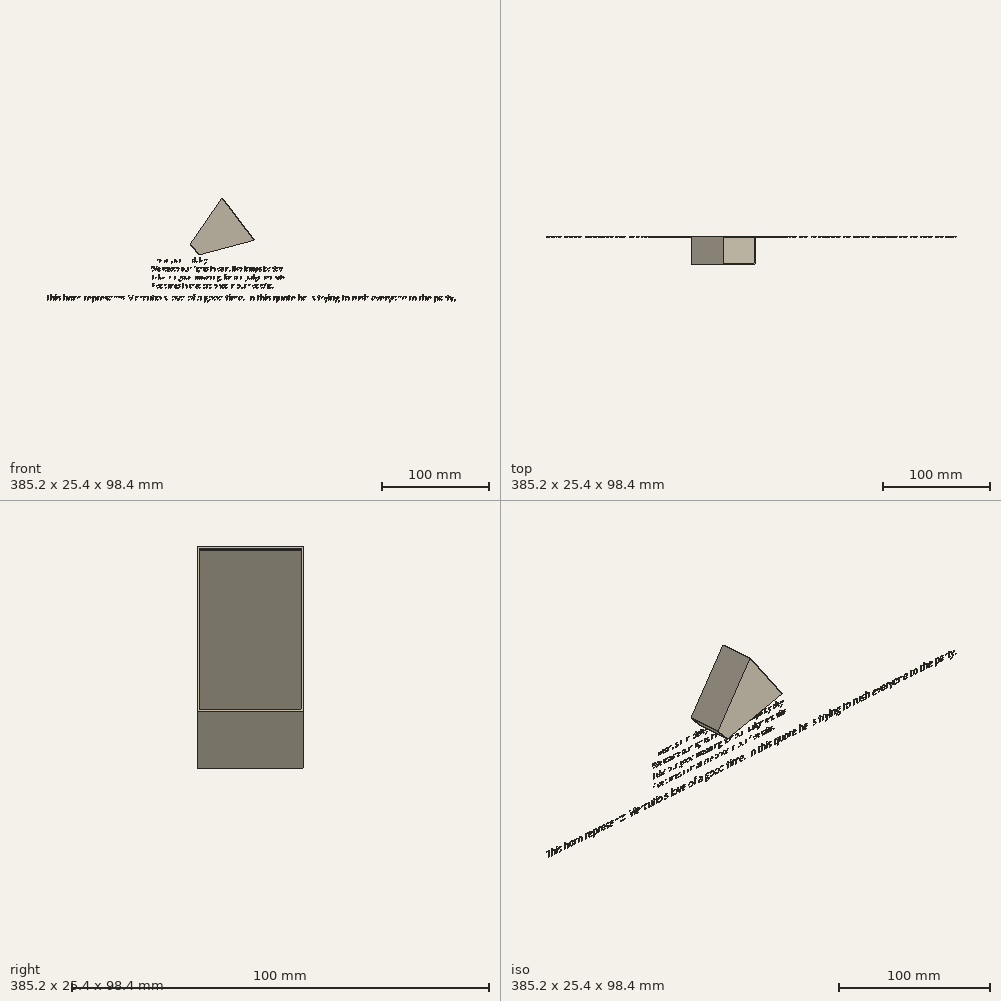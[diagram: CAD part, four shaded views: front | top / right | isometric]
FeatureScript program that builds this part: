
annotation { "Feature Type Name" : "Feature", "Feature Type Description" : "" }
export const myFeature = defineFeature(function(context is Context, id is Id, definition is map)
    precondition{}
    {
        {
            var Q0;
            Q0=qCreatedBy(makeId("Front.planeOp"),FACE);
            var sketch = newSketch(context, id + "F0", { "sketchPlane" : qUnion([Q0])});
            skLineSegment(sketch, "E0", {"start": v(-35.2, 9.6) * mm, "end": v(-26.26, 0) * mm});
            skLineSegment(sketch, "E1", {"start": v(-4.95, 53.37) * mm, "end": v(25.14, 13.72) * mm});
            skLineSegment(sketch, "E2", {"start": v(25.14, 13.72) * mm, "end": v(-26.26, 0) * mm});
            skLineSegment(sketch, "E3", {"start": v(-35.2, 9.6) * mm, "end": v(-4.95, 53.37) * mm});
            skSolve(sketch);
        }
        {
            var Q0;
            Q0=makeQuery(id+"F0.imprint","IMPRINT",FACE,{"disambiguationData":[TD([[makeQuery(id+"F0.imprint","IMPRINT",EDGE,{"derivedFrom":sQuery(id+"F0.wireOp",EDGE,"E0")}),1.0]])]});
            extrude(context, id + "F1", {"entities" : qUnion([Q0]), "depth" : 25.4 * mm, "offsetDistance" : 25.4 * mm});
        }
        {
            var Q0;
            Q0=makeQuery(id+"F1.opExtrude","CAP_FACE",FACE,{"disambiguationData":[OSD([sQuery(id+"F0.wireOp",EDGE,"E0"),sQuery(id+"F0.wireOp",EDGE,"E1"),sQuery(id+"F0.wireOp",EDGE,"E2"),sQuery(id+"F0.wireOp",EDGE,"E3")])],"isStart":false});
            var Q1;
            Q1=makeQuery(id+"F1.opExtrude","SWEPT_FACE",FACE,{"disambiguationData":[OSD([sQuery(id+"F0.wireOp",EDGE,"E1")])]});
            var Q2;
            Q2=makeQuery(id+"F1.opExtrude","SWEPT_FACE",FACE,{"disambiguationData":[OSD([sQuery(id+"F0.wireOp",EDGE,"E2")])]});
            var Q3;
            Q3=makeQuery(id+"F1.opExtrude","SWEPT_FACE",FACE,{"disambiguationData":[OSD([sQuery(id+"F0.wireOp",EDGE,"E3")])]});
            var Q4;
            Q4=makeQuery(id+"F1.opExtrude","SWEPT_FACE",FACE,{"disambiguationData":[OSD([sQuery(id+"F0.wireOp",EDGE,"E0")])]});
            var Q5;
            Q5=makeQuery(id+"F1.opExtrude","CAP_FACE",FACE,{"disambiguationData":[OSD([sQuery(id+"F0.wireOp",EDGE,"E0"),sQuery(id+"F0.wireOp",EDGE,"E1"),sQuery(id+"F0.wireOp",EDGE,"E2"),sQuery(id+"F0.wireOp",EDGE,"E3")])],"isStart":true});
            var Q6;
            Q6=makeQuery(id+"F1.opExtrude","SWEPT_BODY",BODY,{"disambiguationData":[OSD([sQuery(id+"F0.wireOp",EDGE,"E0"),sQuery(id+"F0.wireOp",EDGE,"E1"),sQuery(id+"F0.wireOp",EDGE,"E2"),sQuery(id+"F0.wireOp",EDGE,"E3")])]});
            shell(context, id + "F2", {"isHollow" : true, "entities" : qUnion([Q0, Q1, Q2, Q3, Q4, Q5]), "parts" : qUnion([Q6]), "thickness" : 0.5 * mm});
        }
        {
            var Q0;
            Q0=makeQuery(id+"F1.opExtrude","SWEPT_FACE",FACE,{"disambiguationData":[OSD([sQuery(id+"F0.wireOp",EDGE,"E1")])]});
            var sketch = newSketch(context, id + "F3", { "sketchPlane" : qUnion([Q0])});
            skLineSegment(sketch, "E4", {"start": v(-24.9, 18.3) * mm, "end": v(-24.9, 45) * mm});
            skLineSegment(sketch, "E5", {"start": v(-24.9, 45) * mm, "end": v(-11.57, 45) * mm});
            skLineSegment(sketch, "E6", {"start": v(-11.57, 45) * mm, "end": v(-0.52, 45) * mm});
            skLineSegment(sketch, "E7", {"start": v(-0.52, 45) * mm, "end": v(-0.52, -3.76) * mm});
            skLineSegment(sketch, "E8", {"start": v(-24.9, 18.3) * mm, "end": v(-24.9, -3.76) * mm});
            skLineSegment(sketch, "E9", {"start": v(-24.9, -3.76) * mm, "end": v(-0.52, -3.76) * mm});
            skSolve(sketch);
        }
        {
            var Q0;
            Q0=makeQuery(id+"F3.imprint","IMPRINT",FACE,{"disambiguationData":[TD([[makeQuery(id+"F3.imprint","IMPRINT",EDGE,{"derivedFrom":sQuery(id+"F3.wireOp",EDGE,"E4")}),-1.0]])]});
            extrude(context, id + "F4", {"entities" : qUnion([Q0]), "operationType" : NewBodyOperationType.REMOVE, "oppositeDirection" : true, "depth" : 0.5 * mm, "offsetDistance" : 25.4 * mm});
        }
        {
            var Q0;
            Q0=qCreatedBy(makeId("Front.planeOp"),FACE);
            var sketch = newSketch(context, id + "F5", { "sketchPlane" : qUnion([Q0])});
            skText(sketch, "E10", { "text": "I mean, sir, in delay \nWe waste our lights in vain, like lamps by day. \nTake our good meaning, for our judgment sits \nFive times in that ere once in our five wits.\n", "fontName": "OpenSans-Regular.ttf"});
            const initialGuessF5  = {"E10": [-0.07153, -0.00719, 1, 0, 0.00424]};
            skSetInitialGuess(sketch, initialGuessF5);
            skSolve(sketch);
        }
        {
            var Q0;
            Q0=qCreatedBy(makeId("Front.planeOp"),FACE);
            var sketch = newSketch(context, id + "F6", { "sketchPlane" : qUnion([Q0])});
            skText(sketch, "E11", { "text": "This horn represents Mercutio\'s love of a good time. In this quote he is trying to rush everyone to the party. ", "fontName": "OpenSans-Regular.ttf"});
            const initialGuessF6  = {"E11": [-0.1711, -0.0432, 1, 0, 0.00557]};
            skSetInitialGuess(sketch, initialGuessF6);
            skSolve(sketch);
        }
        {
            var Q0;
            Q0 = qSketchRegion(id + "F5", true);
            var Q1;
            Q1 = qSketchRegion(id + "F6", true);
            var Q2;
            Q2 = qSketchRegion(id + "F6", true);
            extrude(context, id + "F7", {"entities" : qUnion([Q0, Q1, Q2]), "depth" : 0.05 * mm, "offsetDistance" : 25.4 * mm});
        }
    });
